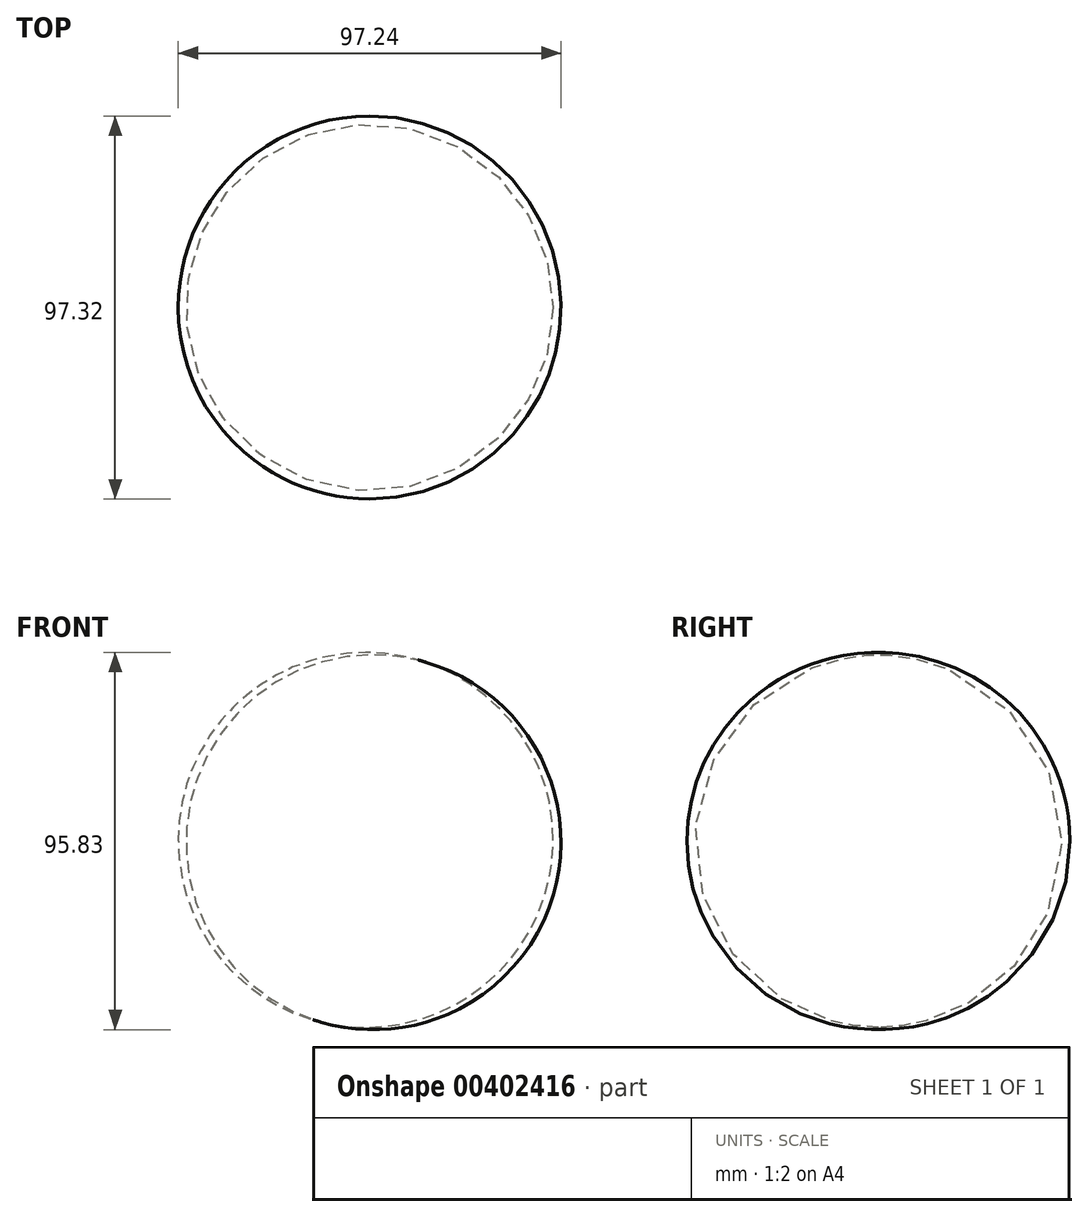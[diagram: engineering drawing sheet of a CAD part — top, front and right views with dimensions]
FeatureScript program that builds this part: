
annotation { "Feature Type Name" : "Feature", "Feature Type Description" : "" }
export const myFeature = defineFeature(function(context is Context, id is Id, definition is map)
    precondition{}
    {
        {
            var Q0;
            Q0=qCreatedBy(makeId("Front.planeOp"),FACE);
            var sketch = newSketch(context, id + "F0", { "sketchPlane" : qUnion([Q0])});
            skArc(sketch, "E0", {"start": v(0, 0) * mm, "mid": v(58.04, 32.7) * mm, "end": v(26.6, 91.44) * mm});
            skLineSegment(sketch, "E1", {"start": v(26.6, 91.44) * mm, "end": v(0, 0) * mm, "construction": true});
            skSolve(sketch);
        }
        {
            var Q0;
            Q0=sQuery(id+"F0.wireOp",EDGE,"E0");
            var Q1;
            Q1=sQuery(id+"F0.wireOp",EDGE,"E1");
            revolve(context, id + "F1", {"bodyType" : ToolBodyType.SURFACE, "surfaceEntities" : qUnion([Q0]), "axis" : qUnion([Q1]), "revolveType" : RevolveType.FULL});
        }
    });
